# Revit family: Sink-Undermount-Kitchen-STERLING-McAllister-32021_1
name_source: partatom
category: Plumbing Fixtures
units: mm (PartAtom-declared; Revit-internal decimal feet)

## family parameters
Cut with Voids When Loaded = No
Host = Face
OmniClass Number = 23.31.13.00
OmniClass Title = Sinks
Part Type = Normal
Room Calculation Point = No
Round Connector Dimension = Use Diameter
Shared = No

## types (1)
- NA-Stainless
    ADA Compliant = Yes
    Assembly Code = D2010400
    CW Connection = No
    Cold Water Inlet = Cold Water Inlet
    Date Modified = 08/25/2022
    Default Elevation = 36"
    Description = SB 24 X 18 X 6 inch ADA
    Drain Included = No
    Finish = Sterling-Metal-NA-Stainless
    HW Connection = No
    Height = 8 1/16"
    Hot Water Inlet = Hot Water Inlet
    Length = 31 3/8"
    Manufacturer = Sterling Co.
    Master Format 2014 = 22 41 16
    Master Format 2014 Name = Residential Lavatories and Sinks
    Material = 18 Guage Stainless Steel
    Model = 32021-NA
    Product Documentation Link = https://resources.kohler.com
    Product Name = McAllister
    Product Page URL = http://www.sterlingplumbing.com
    Type = 1
    URL = https://www.sterlingplumbing.com
    Vent Connection = No
    Waste Connection = Yes
    Waste Water Outlet 1 = Waste Water Outlet 1
    Waste Water Outlet 2 = Waste Water Outlet 2
    WaterSense Certified = No
    Width = 18 5/16"

## geometry (parser evidence)
native form markers: Sweep x4
no freeform markers — native parametric forms only
